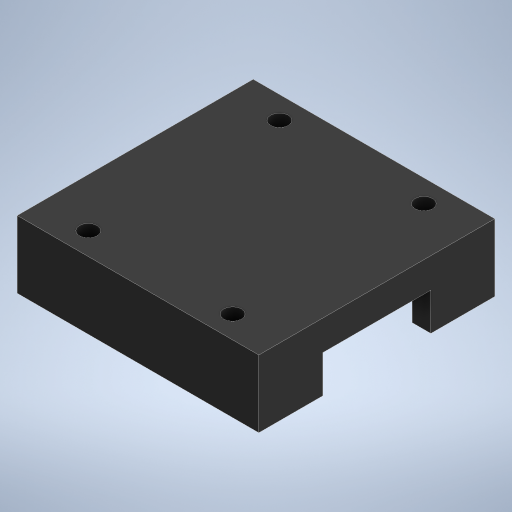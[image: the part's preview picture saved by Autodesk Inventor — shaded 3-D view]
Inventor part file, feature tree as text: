
AUTODESK INVENTOR PART (.ipt)
format: ipt  version: 2024 (Build 280153000, 153)  size: 318,464 bytes
history: native  units: in
note: dims shown in document units (in); Inventor stores cm internally (conversion verified against a paired STEP export)
features: extrude x4, projected_geometry x4, sketch x3, other x1
ambient origin geometry x8: Origin, YZ Plane, XZ Plane, XY Plane, X Axis, Y Axis, Z Axis, Center Point
bodies: Solid1 (feature_tree)
feature tree (12):
  other  "ESC_Mount.ipt"
  extrude  "Extrusion1"  Depth=0.25in TaperAngle=0.0deg
  extrude  "Extrusion2"  Depth=0.25in
  extrude  "Extrusion3"  Depth=0.25in
  extrude  "Extrusion4"  Depth=0.125in
  sketch  "Sketch2"  dims[d0=0.3937in d1=0.25in d2=0.0in]
  projected_geometry  "Projected Loop1"
  sketch  "Sketch3"  dims[d3=0.25in d4=0.25in]
  projected_geometry  "Projected Loop2"
  projected_geometry  "Projected Loop3"
  sketch  "Sketch4"  dims[d5=0.25in d6=0.25in d7=0.125in d8=0.2in d9=0.0in d10=0.1in d11=0.0in d12=0.1181in d13=0.1181in d14=0.1181in d15=0.1181in d16=0.1in d17=0.0in]
  projected_geometry  "Projected Loop4"
